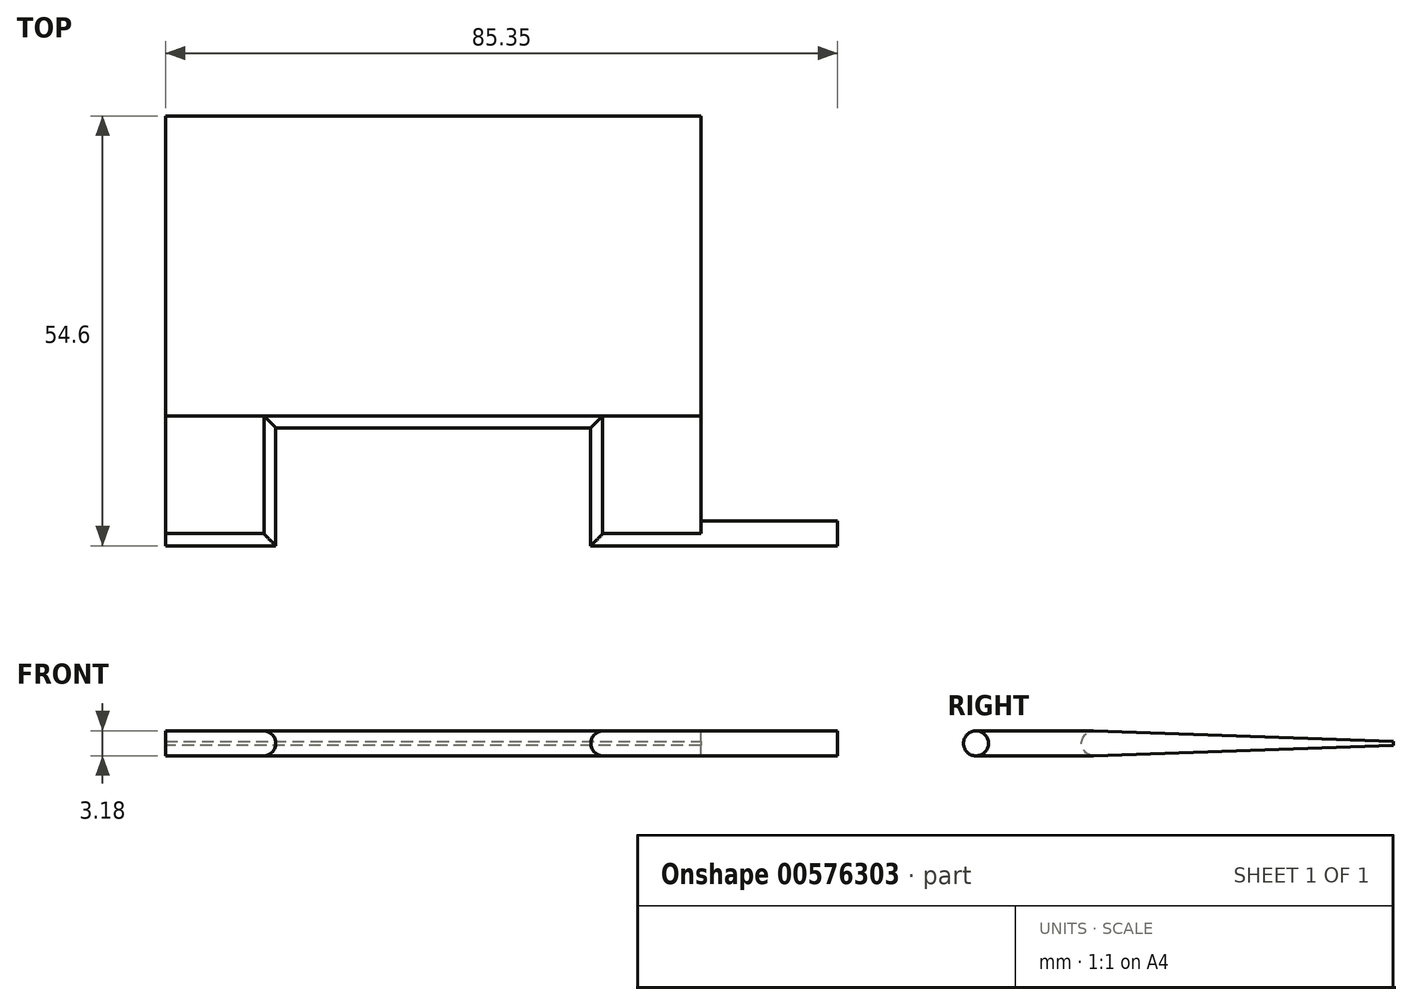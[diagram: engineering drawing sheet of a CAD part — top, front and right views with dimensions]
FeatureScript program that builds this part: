
annotation { "Feature Type Name" : "Feature", "Feature Type Description" : "" }
export const myFeature = defineFeature(function(context is Context, id is Id, definition is map)
    precondition{}
    {
        {
            var Q0;
            Q0=qCreatedBy(makeId("Top.planeOp"),FACE);
            var sketch = newSketch(context, id + "F0", { "sketchPlane" : qUnion([Q0])});
            skLineSegment(sketch, "E0", {"start": v(0, 0) * mm, "end": v(-25, 0) * mm});
            skLineSegment(sketch, "E1", {"start": v(-25, 0) * mm, "end": v(-25, 15) * mm});
            skLineSegment(sketch, "E2", {"start": v(-25, 15) * mm, "end": v(-65, 15) * mm});
            skLineSegment(sketch, "E3", {"start": v(-65, 0) * mm, "end": v(-65, 15) * mm});
            skLineSegment(sketch, "E4", {"start": v(-65, 0) * mm, "end": v(-79, 0) * mm});
            skLineSegment(sketch, "E5.0", {"start": v(-68.17, 3.18) * mm, "end": v(-79, 3.18) * mm});
            skLineSegment(sketch, "E5.1", {"start": v(0, 3.18) * mm, "end": v(-21.82, 3.17) * mm});
            skLineSegment(sketch, "E5.2", {"start": v(-21.82, 3.17) * mm, "end": v(-21.82, 18.18) * mm});
            skLineSegment(sketch, "E5.3", {"start": v(-21.83, 18.18) * mm, "end": v(-68.17, 18.17) * mm});
            skLineSegment(sketch, "E5.4", {"start": v(-68.17, 3.18) * mm, "end": v(-68.17, 18.17) * mm});
            skLineSegment(sketch, "E6", {"start": v(-79, 3.18) * mm, "end": v(-79, 0) * mm});
            skLineSegment(sketch, "E7", {"start": v(0, 3.18) * mm, "end": v(0, 0) * mm});
            skSolve(sketch);
        }
        {
            var Q0;
            Q0=makeQuery(id+"F0.imprint","IMPRINT",FACE,{"disambiguationData":[TD([[makeQuery(id+"F0.imprint","IMPRINT",EDGE,{"derivedFrom":sQuery(id+"F0.wireOp",EDGE,"E0")}),-1.0]])]});
            extrude(context, id + "F1", {"entities" : qUnion([Q0]), "depth" : 3.17 * mm, "offsetDistance" : 25.4 * mm});
        }
        {
            var Q0;
            Q0=makeQuery(id+"F1.opExtrude","CAP_EDGE",EDGE,{"disambiguationData":[OSD([sQuery(id+"F0.wireOp",EDGE,"E5.0")])],"isStart":false});
            var Q1;
            Q1=makeQuery(id+"F1.opExtrude","CAP_EDGE",EDGE,{"disambiguationData":[OSD([sQuery(id+"F0.wireOp",EDGE,"E4")])],"isStart":false});
            var Q2;
            Q2=makeQuery(id+"F1.opExtrude","CAP_EDGE",EDGE,{"disambiguationData":[OSD([sQuery(id+"F0.wireOp",EDGE,"E4")])],"isStart":true});
            var Q3;
            Q3=makeQuery(id+"F1.opExtrude","CAP_EDGE",EDGE,{"disambiguationData":[OSD([sQuery(id+"F0.wireOp",EDGE,"E3")])],"isStart":false});
            var Q4;
            Q4=makeQuery(id+"F1.opExtrude","CAP_EDGE",EDGE,{"disambiguationData":[OSD([sQuery(id+"F0.wireOp",EDGE,"E5.4")])],"isStart":false});
            var Q5;
            Q5=makeQuery(id+"F1.opExtrude","CAP_EDGE",EDGE,{"disambiguationData":[OSD([sQuery(id+"F0.wireOp",EDGE,"E5.4")])],"isStart":true});
            var Q6;
            Q6=makeQuery(id+"F1.opExtrude","CAP_EDGE",EDGE,{"disambiguationData":[OSD([sQuery(id+"F0.wireOp",EDGE,"E5.3")])],"isStart":false});
            var Q7;
            Q7=makeQuery(id+"F1.opExtrude","CAP_EDGE",EDGE,{"disambiguationData":[OSD([sQuery(id+"F0.wireOp",EDGE,"E2")])],"isStart":false});
            var Q8;
            Q8=makeQuery(id+"F1.opExtrude","CAP_EDGE",EDGE,{"disambiguationData":[OSD([sQuery(id+"F0.wireOp",EDGE,"E2")])],"isStart":true});
            var Q9;
            Q9=makeQuery(id+"F1.opExtrude","CAP_EDGE",EDGE,{"disambiguationData":[OSD([sQuery(id+"F0.wireOp",EDGE,"E5.0")])],"isStart":true});
            var Q10;
            Q10=makeQuery(id+"F1.opExtrude","CAP_EDGE",EDGE,{"disambiguationData":[OSD([sQuery(id+"F0.wireOp",EDGE,"E3")])],"isStart":true});
            var Q11;
            Q11=makeQuery(id+"F1.opExtrude","CAP_EDGE",EDGE,{"disambiguationData":[OSD([sQuery(id+"F0.wireOp",EDGE,"E5.3")])],"isStart":true});
            var Q12;
            Q12=makeQuery(id+"F1.opExtrude","CAP_EDGE",EDGE,{"disambiguationData":[OSD([sQuery(id+"F0.wireOp",EDGE,"E1")])],"isStart":true});
            var Q13;
            Q13=makeQuery(id+"F1.opExtrude","CAP_EDGE",EDGE,{"disambiguationData":[OSD([sQuery(id+"F0.wireOp",EDGE,"E1")])],"isStart":false});
            var Q14;
            Q14=makeQuery(id+"F1.opExtrude","CAP_EDGE",EDGE,{"disambiguationData":[OSD([sQuery(id+"F0.wireOp",EDGE,"E5.2")])],"isStart":false});
            var Q15;
            Q15=makeQuery(id+"F1.opExtrude","CAP_EDGE",EDGE,{"disambiguationData":[OSD([sQuery(id+"F0.wireOp",EDGE,"E5.1")])],"isStart":false});
            var Q16;
            Q16=makeQuery(id+"F1.opExtrude","CAP_EDGE",EDGE,{"disambiguationData":[OSD([sQuery(id+"F0.wireOp",EDGE,"E5.1")])],"isStart":true});
            var Q17;
            Q17=makeQuery(id+"F1.opExtrude","CAP_EDGE",EDGE,{"disambiguationData":[OSD([sQuery(id+"F0.wireOp",EDGE,"E0")])],"isStart":false});
            var Q18;
            Q18=makeQuery(id+"F1.opExtrude","CAP_EDGE",EDGE,{"disambiguationData":[OSD([sQuery(id+"F0.wireOp",EDGE,"E0")])],"isStart":true});
            var Q19;
            Q19=makeQuery(id+"F1.opExtrude","CAP_EDGE",EDGE,{"disambiguationData":[OSD([sQuery(id+"F0.wireOp",EDGE,"E5.2")])],"isStart":true});
            fillet(context, id + "F2", {"entities" : qUnion([Q0, Q1, Q2, Q3, Q4, Q5, Q6, Q7, Q8, Q9, Q10, Q11, Q12, Q13, Q14, Q15, Q16, Q17, Q18, Q19]), "radius" : 1.59 * mm, "tangentPropagation" : true, "allowEdgeOverflow" : false});
        }
        {
            var Q0;
            Q0=qCreatedBy(makeId("Front.planeOp"),FACE);
            cPlane(context, id + "F3", {"entities" : qUnion([Q0]), "cplaneType" : CPlaneType.OFFSET, "offset" : 1.6 * mm, "oppositeDirection" : true, "width" : 152.4 * mm, "height" : 152.4 * mm});
        }
        {
            var Q0;
            Q0=qCreatedBy(id+"F3.planeOp",FACE);
            var sketch = newSketch(context, id + "F4", { "sketchPlane" : qUnion([Q0])});
            skLineSegment(sketch, "E8.top", {"start": v(-11, 3.18) * mm, "end": v(-23.5, 3.18) * mm});
            skLineSegment(sketch, "E8.right", {"start": v(-23.5, 0) * mm, "end": v(-23.5, 3.18) * mm});
            skLineSegment(sketch, "E9.top", {"start": v(-79, 0) * mm, "end": v(-66.5, 0) * mm});
            skLineSegment(sketch, "E9.right", {"start": v(-66.5, 3.18) * mm, "end": v(-66.5, 0) * mm});
            skLineSegment(sketch, "E10", {"start": v(-23.5, 0) * mm, "end": v(-11, 0) * mm});
            skLineSegment(sketch, "E11", {"start": v(-11, 0) * mm, "end": v(-11, 3.18) * mm});
            skLineSegment(sketch, "E12", {"start": v(-79, 0) * mm, "end": v(-79, 3.18) * mm});
            skLineSegment(sketch, "E13", {"start": v(-79, 3.18) * mm, "end": v(-66.5, 3.18) * mm});
            skSolve(sketch);
        }
        {
            var Q0;
            Q0=qCreatedBy(makeId("Front.planeOp"),FACE);
            cPlane(context, id + "F5", {"entities" : qUnion([Q0]), "cplaneType" : CPlaneType.OFFSET, "offset" : 16.5 * mm, "oppositeDirection" : true, "width" : 152.4 * mm, "height" : 152.4 * mm});
        }
        {
            var Q0;
            Q0 = qSketchRegion(id + "F4", true);
            extrude(context, id + "F6", {"entities" : qUnion([Q0]), "operationType" : NewBodyOperationType.ADD, "oppositeDirection" : true, "depth" : 15 * mm + 3.17 * mm, "offsetDistance" : 25.4 * mm});
        }
        {
            var Q0;
            Q0=qCreatedBy(id+"F5.planeOp",FACE);
            var sketch = newSketch(context, id + "F7", { "sketchPlane" : qUnion([Q0])});
            skLineSegment(sketch, "E14", {"start": v(-79, 3.17) * mm, "end": v(-79, 0) * mm});
            skLineSegment(sketch, "E15", {"start": v(0, 0) * mm, "end": v(-11, 0) * mm});
            skLineSegment(sketch, "E16", {"start": v(-11, 0) * mm, "end": v(-79, 0) * mm});
            skLineSegment(sketch, "E17", {"start": v(-79, 3.17) * mm, "end": v(-11, 3.18) * mm});
            skLineSegment(sketch, "E18", {"start": v(-11, 3.18) * mm, "end": v(-11, 0) * mm});
            skSolve(sketch);
        }
        {
            var Q0;
            Q0 = qSketchRegion(id + "F7", true);
            extrude(context, id + "F8", {"entities" : qUnion([Q0]), "operationType" : NewBodyOperationType.ADD, "oppositeDirection" : true, "depth" : 38.1 * mm, "offsetDistance" : 25.4 * mm});
        }
        {
            var Q0;
            Q0=qCreatedBy(makeId("Right.planeOp"),FACE);
            var sketch = newSketch(context, id + "F9", { "sketchPlane" : qUnion([Q0])});
            skCircle(sketch, "E19", {"center": v(1.59, 1.59) * mm, "radius": 1.59 * mm});
            skSolve(sketch);
        }
        {
            var Q0;
            Q0 = qSketchRegion(id + "F9", true);
            extrude(context, id + "F10", {"entities" : qUnion([Q0]), "operationType" : NewBodyOperationType.ADD, "depth" : 6.35 * mm, "offsetDistance" : 25.4 * mm});
        }
        {
            var Q0;
            Q0=makeQuery(id+"F8.opExtrude","CAP_EDGE",EDGE,{"disambiguationData":[OSD([sQuery(id+"F7.wireOp",EDGE,"E17")])],"isStart":false});
            var Q1;
            Q1=makeQuery(id+"F8.opExtrude","CAP_EDGE",EDGE,{"disambiguationData":[OSD([sQuery(id+"F7.wireOp",EDGE,"E16")])],"isStart":false});
            chamfer(context, id + "F11", {"entities" : qUnion([Q0, Q1]), "chamferType" : ChamferType.OFFSET_ANGLE, "width" : 38.1 * mm, "oppositeDirection" : true, "angle" : 2 * degree, "tangentPropagation" : true});
        }
    });
